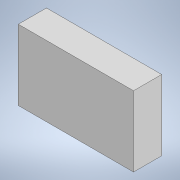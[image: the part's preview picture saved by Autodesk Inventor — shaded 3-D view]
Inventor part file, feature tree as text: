
AUTODESK INVENTOR PART (.ipt)
format: ipt  version: 2020 (Build 240168000, 168)  size: 88,064 bytes
history: native  units: mm
features: extrude x1
ambient origin geometry x8: Origin, YZ Plane, XZ Plane, XY Plane, X Axis, Y Axis, Z Axis, Center Point
bodies: Solide1 (feature_tree)
feature tree (1):
  extrude  "Extrusion1"  Depth=90.0mm
